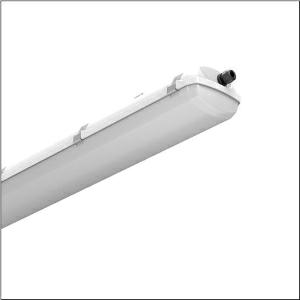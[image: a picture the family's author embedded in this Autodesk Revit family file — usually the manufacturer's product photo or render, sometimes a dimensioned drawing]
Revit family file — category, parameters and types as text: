
# Revit family: monsun_r__ex_51fxa27l860a3g_f971
name_source: partatom
category: Lighting Fixtures
units: mm (PartAtom-declared; Revit-internal decimal feet)

## family parameters
Cut with Voids When Loaded = No
Host = Face
Light Source = No
Part Type = Normal
Room Calculation Point = No
Round Connector Dimension = Use Diameter
Shared = No

## types (1)
- --- (1 x LED, 6560 lm, 53 W, 6500K)
    Apparent Load = 53 VA
    CIE Flux Codes = 46 76 94 98 100
    Color Rendering = 80
    Color Temperature = 6500K
    Default Elevation = 1800 mm
    Description = Monsun® Ex, damp-proof luminaire, primary optical cover: cover, of PC, UV-stabilised, opal, light emission: direct distribution, primary light characteristic: symmetric, installation type: surface-mounted, LED, rated luminous flux: 6.560lm, luminous efficacy: 124lm/W, light colour: 860, colour temperature: 6000K, control gear: ECG, with terminal, 3+1-pole, max. 2.5mm², through-wiring: 6x 2.5mm², mains connection: 220..250V, AC, 50/60Hz, rated input power: 53W, control gear: single battery element, housing, of PC, light grey (RAL 7035), incl. 1x Ex cable gland M20 for cable diameter 7..12mm with sealing, incl. 1x Ex locking screw M20 with sealing, length: 1.280mm, width: 155mm, height: 105mm, clip for enclosure, of stainless steel, protection rating (complete): IP66, insulation class (complete): insulation class I (protective earthing), certification: CE, explosion class: zone 1,21 II 2G Ex eb mb op is IIC T4 Gb, II 2D Ex tb op is IIIC T67°C Db, impact resistance: IK10, permissible operating ambient temperature: 0..+35°C, contact your sales advisor before using the luminaires in applications with unclear chemical exposure, large temperature fluctuations or condensation-forming humidity, packaging unit: 1 piece
    Height = 105 mm
    Lamp = 1 x LED
    Lamp Light Flux = 6560 lm
    Lamp Power = 53 W
    Lamp count = 1
    Length = 1280 mm
    Luminous efficacy = 124 lm/W
    Manufacturer = Siteco
    ModVariant = No
    Model = 51FXA27L860A3G
    Mounting Place = Ceiling
    Mounting Type = Surface mounted
    Number of Poles = 1
    OnlyDefault = Yes
    Power Factor = 1
    Product Name = Monsun® Ex
    Product group = damp-proof luminaire
    ProductGroupID = 301
    Protection Class = Protection class I
    Protection Degree = IP 66
    RLX_Detail_Level = 1
    RLX_Emergency_Light_Flux = 0 lm
    RLX_Emergency_Type = 0
    RLX_Emergency_Type_DB = No
    RlxData = <blob elided: 41637 chars, md5=0c9ef37d>
    Socket = socket
    Standby Power = 0 W
    System Light Flux = 6560 lm
    System Power = 53 W
    Type Comments = -
    Type Image = l_1258882.jpg
    URL = http://relux.com
    VarID = @adj_022337
    Voltage = 0 V
    Weight = 0.00 kg
    Width = 155 mm

## geometry (parser evidence)
native form markers: Blend x4, Sweep x9
no freeform markers — native parametric forms only
